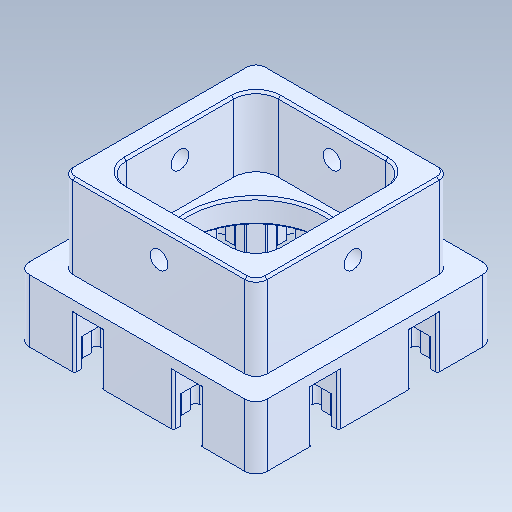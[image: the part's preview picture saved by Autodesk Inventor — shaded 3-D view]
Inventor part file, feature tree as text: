
AUTODESK INVENTOR PART (.ipt)
format: ipt  version: 2020 (Build 240168000, 168)  size: 313,344 bytes
history: native  units: in
note: dims shown in document units (in); Inventor stores cm internally (conversion verified against a paired STEP export)
features: fillet x1
ambient origin geometry x8: Origin, YZ Plane, XZ Plane, XY Plane, X Axis, Y Axis, Z Axis, Center Point
bodies: Solid1 (feature_tree)
feature tree (1):
  fillet  "Fillet5"  [1 undecoded]
note: 1 required parameter value undecoded (feature->parameter linkage not recoverable at this tier; creation-order binding heuristic only, values carry confidence <= 0.55)
